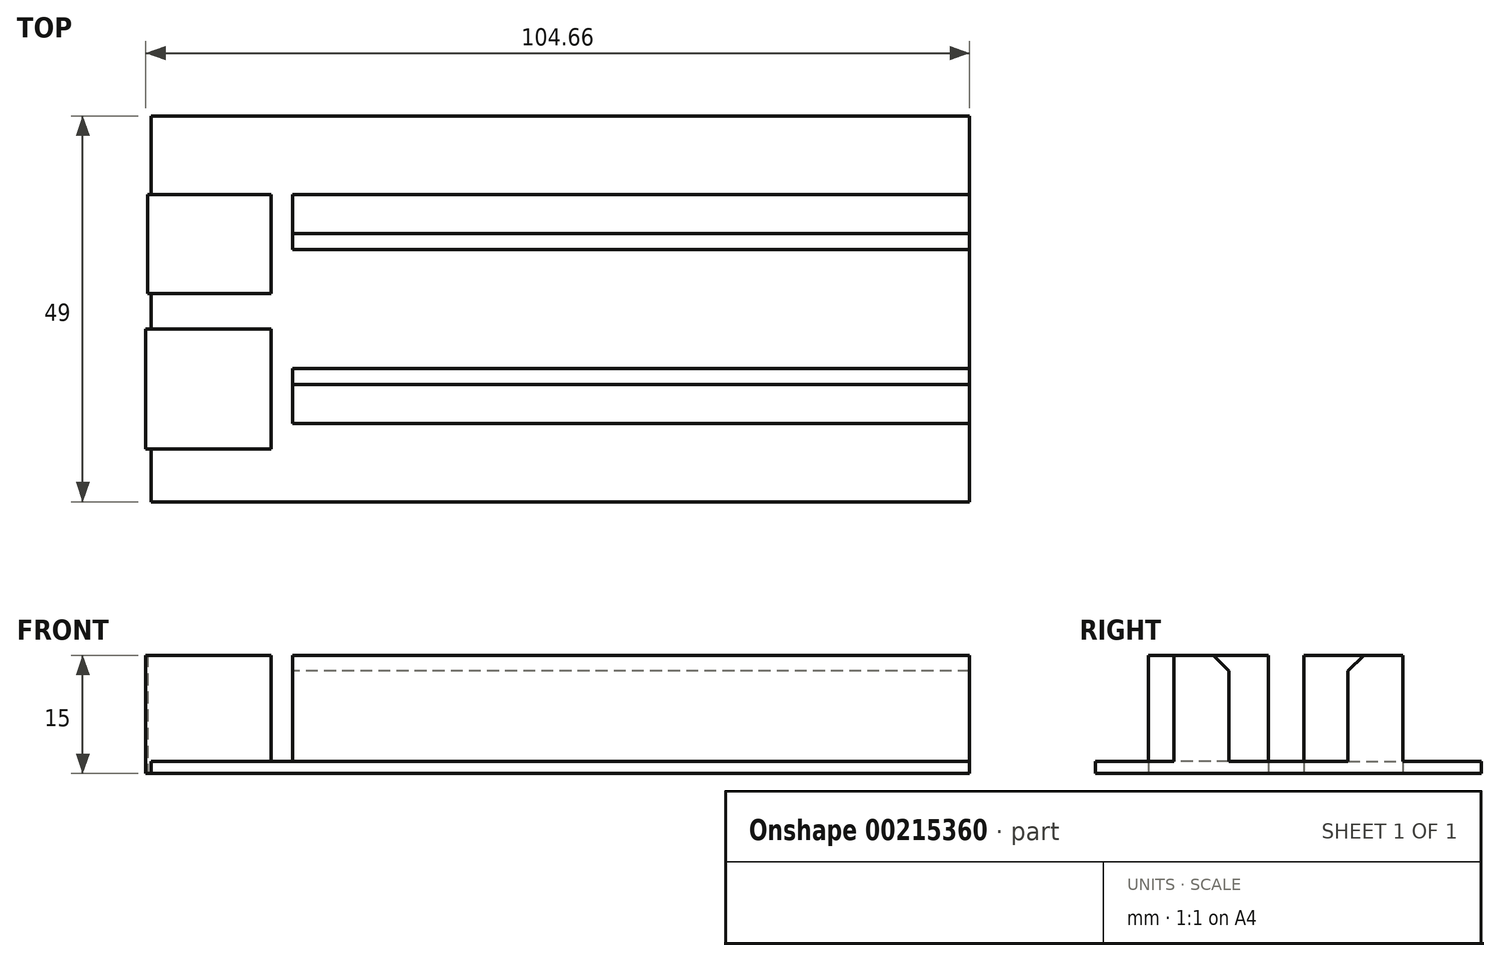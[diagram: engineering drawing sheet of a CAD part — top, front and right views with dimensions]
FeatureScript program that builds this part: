
annotation { "Feature Type Name" : "Feature", "Feature Type Description" : "" }
export const myFeature = defineFeature(function(context is Context, id is Id, definition is map)
    precondition{}
    {
        {
            var Q0;
            Q0=qCreatedBy(makeId("Top.planeOp"),FACE);
            var sketch = newSketch(context, id + "F0", { "sketchPlane" : qUnion([Q0])});
            skLineSegment(sketch, "E0.bottom", {"start": v(52, 24.5) * mm, "end": v(-52, 24.5) * mm});
            skLineSegment(sketch, "E0.top", {"start": v(52, -24.5) * mm, "end": v(-52, -24.5) * mm});
            skLineSegment(sketch, "E0.left", {"start": v(52, 24.5) * mm, "end": v(52, -24.5) * mm});
            skLineSegment(sketch, "E0.right", {"start": v(-52, 24.5) * mm, "end": v(-52, -24.5) * mm});
            skPoint(sketch, "E0.middle", {"position": v(0, 0) * mm});
            skLineSegment(sketch, "E1.bottom", {"start": v(-36.71, 14.53) * mm, "end": v(-52.43, 14.53) * mm});
            skLineSegment(sketch, "E1.top", {"start": v(-36.71, 1.95) * mm, "end": v(-52.43, 1.95) * mm});
            skLineSegment(sketch, "E1.left", {"start": v(-36.71, 14.53) * mm, "end": v(-36.71, 1.95) * mm});
            skLineSegment(sketch, "E1.right", {"start": v(-52.43, 14.53) * mm, "end": v(-52.43, 1.95) * mm});
            skPoint(sketch, "E1.middle", {"position": v(-44.57, 8.24) * mm});
            skLineSegment(sketch, "E2.bottom", {"start": v(-36.71, -2.54) * mm, "end": v(-52.66, -2.54) * mm});
            skLineSegment(sketch, "E2.top", {"start": v(-36.71, -17.81) * mm, "end": v(-52.66, -17.81) * mm});
            skLineSegment(sketch, "E2.left", {"start": v(-36.71, -2.54) * mm, "end": v(-36.71, -17.81) * mm});
            skLineSegment(sketch, "E2.right", {"start": v(-52.66, -2.54) * mm, "end": v(-52.66, -17.81) * mm});
            skPoint(sketch, "E2.middle", {"position": v(-44.68, -10.17) * mm});
            skLineSegment(sketch, "E3.bottom", {"start": v(-34.02, 14.53) * mm, "end": v(52, 14.53) * mm});
            skLineSegment(sketch, "E3.top", {"start": v(-34.02, 7.57) * mm, "end": v(52, 7.57) * mm});
            skLineSegment(sketch, "E3.left", {"start": v(-34.02, 14.53) * mm, "end": v(-34.02, 7.57) * mm});
            skLineSegment(sketch, "E3.right", {"start": v(52, 14.53) * mm, "end": v(52, 7.57) * mm});
            skLineSegment(sketch, "E4", {"start": v(0, 0) * mm, "end": v(23.03, 0) * mm, "construction": true});
            skLineSegment(sketch, "E5.MirrorCS", {"start": v(-34.02, -7.57) * mm, "end": v(52, -7.57) * mm});
            skLineSegment(sketch, "E6.MirrorCS", {"start": v(-34.02, -14.53) * mm, "end": v(-34.02, -7.57) * mm});
            skLineSegment(sketch, "E7.MirrorCS", {"start": v(52, -14.53) * mm, "end": v(52, -7.57) * mm});
            skLineSegment(sketch, "E8.MirrorCS", {"start": v(-34.02, -14.53) * mm, "end": v(52, -14.53) * mm});
            skSolve(sketch);
        }
        {
            var Q0;
            {var subQ5=sQuery(id+"F0.wireOp",EDGE,"E0.bottom");Q0=makeQuery(id+"F0.imprint","IMPRINT",FACE,{"disambiguationData":[TD([[makeQuery(id+"F0.imprint","IMPRINT",EDGE,{"derivedFrom":subQ5}),1.0]])]});}
            var Q1;
            {var subQ5=sQuery(id+"F0.wireOp",EDGE,"E2.left");Q1=makeQuery(id+"F0.imprint","IMPRINT",FACE,{"disambiguationData":[TD([[makeQuery(id+"F0.imprint","IMPRINT",EDGE,{"derivedFrom":subQ5}),-1.0]])]});}
            var Q2;
            {var subQ5=sQuery(id+"F0.wireOp",EDGE,"E1.left");Q2=makeQuery(id+"F0.imprint","IMPRINT",FACE,{"disambiguationData":[TD([[makeQuery(id+"F0.imprint","IMPRINT",EDGE,{"derivedFrom":subQ5}),-1.0]])]});}
            var Q3;
            Q3=makeQuery(id+"F0.imprint","IMPRINT",FACE,{"disambiguationData":[TD([[makeQuery(id+"F0.imprint","IMPRINT",EDGE,{"derivedFrom":sQuery(id+"F0.wireOp",EDGE,"E3.bottom")}),-1.0]])]});
            var Q4;
            Q4=makeQuery(id+"F0.imprint","IMPRINT",FACE,{"disambiguationData":[TD([[makeQuery(id+"F0.imprint","IMPRINT",EDGE,{"derivedFrom":sQuery(id+"F0.wireOp",EDGE,"E5.MirrorCS")}),-1.0]])]});
            extrude(context, id + "F1", {"entities" : qUnion([Q0, Q1, Q2, Q3, Q4]), "depth" : 1.5 * mm});
        }
        {
            var Q0;
            {var subQ5=sQuery(id+"F0.wireOp",EDGE,"E1.left");Q0=makeQuery(id+"F0.imprint","IMPRINT",FACE,{"disambiguationData":[TD([[makeQuery(id+"F0.imprint","IMPRINT",EDGE,{"derivedFrom":subQ5}),-1.0]])]});}
            var Q1;
            {var subQ5=sQuery(id+"F0.wireOp",EDGE,"E2.left");Q1=makeQuery(id+"F0.imprint","IMPRINT",FACE,{"disambiguationData":[TD([[makeQuery(id+"F0.imprint","IMPRINT",EDGE,{"derivedFrom":subQ5}),-1.0]])]});}
            var Q2;
            {var subQ5=sQuery(id+"F0.wireOp",EDGE,"E2.right");Q2=makeQuery(id+"F0.imprint","IMPRINT",FACE,{"disambiguationData":[TD([[makeQuery(id+"F0.imprint","IMPRINT",EDGE,{"derivedFrom":subQ5}),1.0]])]});}
            var Q3;
            {var subQ5=sQuery(id+"F0.wireOp",EDGE,"E1.right");Q3=makeQuery(id+"F0.imprint","IMPRINT",FACE,{"disambiguationData":[TD([[makeQuery(id+"F0.imprint","IMPRINT",EDGE,{"derivedFrom":subQ5}),1.0]])]});}
            var Q4;
            Q4=makeQuery(id+"F0.imprint","IMPRINT",FACE,{"disambiguationData":[TD([[makeQuery(id+"F0.imprint","IMPRINT",EDGE,{"derivedFrom":sQuery(id+"F0.wireOp",EDGE,"E3.bottom")}),-1.0]])]});
            var Q5;
            Q5=makeQuery(id+"F0.imprint","IMPRINT",FACE,{"disambiguationData":[TD([[makeQuery(id+"F0.imprint","IMPRINT",EDGE,{"derivedFrom":sQuery(id+"F0.wireOp",EDGE,"E5.MirrorCS")}),-1.0]])]});
            extrude(context, id + "F2", {"entities" : qUnion([Q0, Q1, Q2, Q3, Q4, Q5]), "operationType" : NewBodyOperationType.ADD, "depth" : 15 * mm});
        }
        {
            var Q0;
            Q0=makeQuery(id+"F2.opExtrude","CAP_EDGE",EDGE,{"disambiguationData":[OSD([sQuery(id+"F0.wireOp",EDGE,"E5.MirrorCS")])],"isStart":false});
            var Q1;
            Q1=makeQuery(id+"F2.opExtrude","CAP_EDGE",EDGE,{"disambiguationData":[OSD([sQuery(id+"F0.wireOp",EDGE,"E3.top")])],"isStart":false});
            chamfer(context, id + "F3", {"entities" : qUnion([Q0, Q1]), "width" : 2 * mm, "tangentPropagation" : true});
        }
    });
